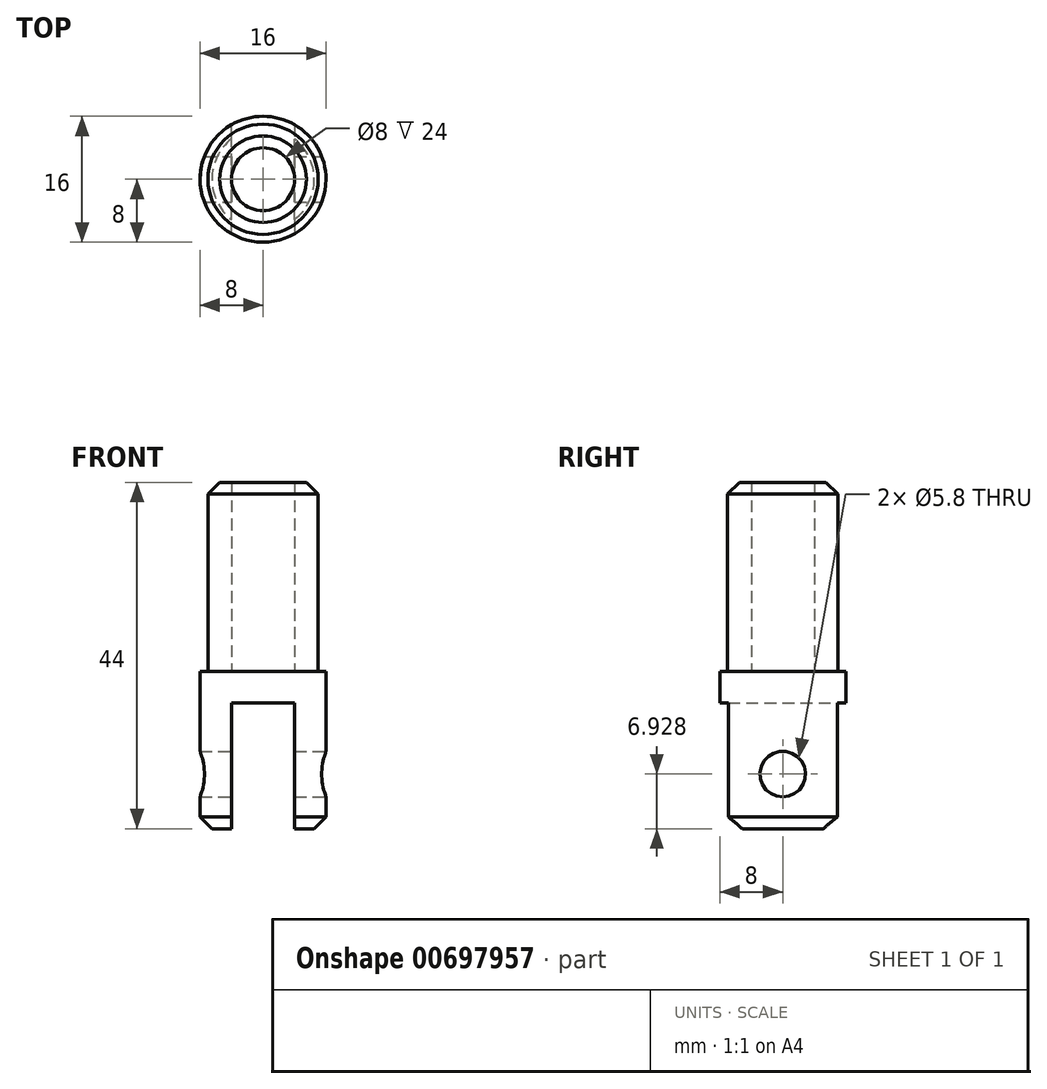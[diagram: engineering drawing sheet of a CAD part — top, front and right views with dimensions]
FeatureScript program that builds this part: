
annotation { "Feature Type Name" : "Feature", "Feature Type Description" : "" }
export const myFeature = defineFeature(function(context is Context, id is Id, definition is map)
    precondition{}
    {
        {
            assignVariable(context, id + "F0", {"name" : "d_r1", "anyValue" : 8});
        }
        {
            assignVariable(context, id + "F1", {"name" : "d_r2", "anyValue" : 14});
        }
        {
            assignVariable(context, id + "F2", {"name" : "d_r3", "anyValue" : 16});
        }
        {
            assignVariable(context, id + "F3", {"name" : "z_r1", "anyValue" : 1});
        }
        {
            assignVariable(context, id + "F4", {"name" : "z_r2", "anyValue" : 25});
        }
        {
            assignVariable(context, id + "F5", {"name" : "z_r3", "anyValue" : 1});
        }
        {
            assignVariable(context, id + "F6", {"name" : "z_baseplate", "anyValue" : 3});
        }
        {
            var Q0;
            Q0=qCreatedBy(makeId("Top.planeOp"),FACE);
            var sketch = newSketch(context, id + "F7", { "sketchPlane" : qUnion([Q0])});
            skCircle(sketch, "E0", {"center": v(0, 0) * mm, "radius": 4 * mm});
            skCircle(sketch, "E1", {"center": v(0, 0) * mm, "radius": 7 * mm});
            skCircle(sketch, "E2", {"center": v(0, 0) * mm, "radius": 8 * mm});
            skSolve(sketch);
        }
        {
            var Q0;
            Q0=makeQuery(id+"F7.imprint","IMPRINT",FACE,{"disambiguationData":[TD([[makeQuery(id+"F7.imprint","IMPRINT",EDGE,{"derivedFrom":sQuery(id+"F7.wireOp",EDGE,"E0")}),-1.0]])]});
            extrude(context, id + "F8", {"entities" : qUnion([Q0]), "depth" : (getVariable(context, 'z_r2')) * mm, "offsetDistance" : 25 * mm});
        }
        {
            var Q0;
            Q0=makeQuery(id+"F7.imprint","IMPRINT",FACE,{"disambiguationData":[TD([[makeQuery(id+"F7.imprint","IMPRINT",EDGE,{"derivedFrom":sQuery(id+"F7.wireOp",EDGE,"E0")}),1.0]])]});
            extrude(context, id + "F9", {"entities" : qUnion([Q0]), "operationType" : NewBodyOperationType.ADD, "depth" : (getVariable(context, 'z_r1')) * mm, "offsetDistance" : 25 * mm});
        }
        {
            var Q0;
            Q0=makeQuery(id+"F7.imprint","IMPRINT",FACE,{"disambiguationData":[TD([[makeQuery(id+"F7.imprint","IMPRINT",EDGE,{"derivedFrom":sQuery(id+"F7.wireOp",EDGE,"E1")}),-1.0]])]});
            extrude(context, id + "F10", {"entities" : qUnion([Q0]), "operationType" : NewBodyOperationType.ADD, "depth" : (getVariable(context, 'z_r3')) * mm, "offsetDistance" : 25 * mm});
        }
        {
            var Q0;
            Q0=makeQuery(id+"F7.imprint","IMPRINT",FACE,{"disambiguationData":[TD([[makeQuery(id+"F7.imprint","IMPRINT",EDGE,{"derivedFrom":sQuery(id+"F7.wireOp",EDGE,"E1")}),-1.0]])]});
            var Q1;
            Q1=makeQuery(id+"F7.imprint","IMPRINT",FACE,{"disambiguationData":[TD([[makeQuery(id+"F7.imprint","IMPRINT",EDGE,{"derivedFrom":sQuery(id+"F7.wireOp",EDGE,"E0")}),-1.0]])]});
            var Q2;
            Q2=makeQuery(id+"F7.imprint","IMPRINT",FACE,{"disambiguationData":[TD([[makeQuery(id+"F7.imprint","IMPRINT",EDGE,{"derivedFrom":sQuery(id+"F7.wireOp",EDGE,"E0")}),1.0]])]});
            extrude(context, id + "F11", {"entities" : qUnion([Q0, Q1, Q2]), "operationType" : NewBodyOperationType.ADD, "oppositeDirection" : true, "depth" : (getVariable(context, 'z_baseplate')) * mm, "offsetDistance" : 25 * mm});
        }
        {
            var Q0;
            Q0=makeQuery(id+"F11.opExtrude","CAP_FACE",FACE,{"disambiguationData":[OSD([sQuery(id+"F7.wireOp",EDGE,"E2")])],"isStart":false});
            var sketch = newSketch(context, id + "F12", { "sketchPlane" : qUnion([Q0])});
            skLineSegment(sketch, "E3", {"start": v(-4, 6.93) * mm, "end": v(-4, -6.93) * mm});
            skLineSegment(sketch, "E4", {"start": v(4, 6.93) * mm, "end": v(4, -6.93) * mm});
            skLineSegment(sketch, "E5", {"start": v(0, 0) * mm, "end": v(-4, 0) * mm, "construction": true});
            skLineSegment(sketch, "E6", {"start": v(0, 0) * mm, "end": v(4, 0) * mm, "construction": true});
            skSolve(sketch);
        }
        {
            var Q0;
            {var subQ0=sQuery(id+"F12.wireOp",EDGE,"E3");Q0=makeQuery(id+"F12.imprint","IMPRINT",FACE,{"disambiguationData":[TD([[makeQuery(id+"F12.imprint","IMPRINT",EDGE,{"derivedFrom":subQ0}),-1.0]])]});}
            var Q1;
            {var subQ0=sQuery(id+"F12.wireOp",EDGE,"E4");Q1=makeQuery(id+"F12.imprint","IMPRINT",FACE,{"disambiguationData":[TD([[makeQuery(id+"F12.imprint","IMPRINT",EDGE,{"derivedFrom":subQ0}),1.0]])]});}
            extrude(context, id + "F13", {"entities" : qUnion([Q0, Q1]), "operationType" : NewBodyOperationType.ADD, "depth" : (getVariable(context, 'd_r3')) * mm, "offsetDistance" : 25 * mm});
        }
        {
            var Q0;
            Q0=qCreatedBy(makeId("Right.planeOp"),FACE);
            var sketch = newSketch(context, id + "F14", { "sketchPlane" : qUnion([Q0])});
            skLineSegment(sketch, "E7.0", {"start": v(-6.93, -19) * mm, "end": v(6.93, -19) * mm});
            skCircle(sketch, "E8", {"center": v(0, -12.07) * mm, "radius": 6.93 * mm});
            skPoint(sketch, "E8.centerSnap0", {"position": v(0, -19) * mm});
            skLineSegment(sketch, "E9.0", {"start": v(-6.93, -19) * mm, "end": v(-6.93, -3) * mm});
            skLineSegment(sketch, "E9.1", {"start": v(6.93, -19) * mm, "end": v(6.93, -3) * mm});
            skLineSegment(sketch, "E10", {"start": v(-6.93, -3) * mm, "end": v(6.93, -3) * mm});
            skCircle(sketch, "E11", {"center": v(0, -12.07) * mm, "radius": 2.9 * mm});
            skSolve(sketch);
        }
        {
            var Q0;
            Q0=makeQuery(id+"F14.imprint","IMPRINT",FACE,{"disambiguationData":[TD([[makeQuery(id+"F14.imprint","IMPRINT",EDGE,{"derivedFrom":sQuery(id+"F14.wireOp",EDGE,"E11")}),1.0]])]});
            extrude(context, id + "F15", {"entities" : qUnion([Q0]), "operationType" : NewBodyOperationType.REMOVE, "endBound" : BoundingType.SYMMETRIC, "oppositeDirection" : true, "depth" : 25 * mm, "offsetDistance" : 25 * mm});
        }
        {
            var Q0;
            Q0=makeQuery(id+"F8.opExtrude","CAP_EDGE",EDGE,{"disambiguationData":[OSD([sQuery(id+"F7.wireOp",EDGE,"E1")])],"isStart":false});
            var Q1;
            Q1=makeQuery(id+"F13.opExtrude","CAP_EDGE",EDGE,{"disambiguationData":[OSD([sQuery(id+"F12.wireOp",EDGE,"E4")])],"isStart":true});
            var Q2;
            Q2=makeQuery(id+"F13.opExtrude","CAP_EDGE",EDGE,{"disambiguationData":[OSD([sQuery(id+"F12.wireOp",EDGE,"E3")])],"isStart":true});
            var Q3;
            {var subQ0=sQuery(id+"F12.wireOp",EDGE,"E4");var subQ1=sQuery(id+"F7.wireOp",EDGE,"E2");var subQ2=makeQuery(id+"F11.opExtrude","CAP_EDGE",EDGE,{"disambiguationData":[OSD([subQ1])],"isStart":false});Q3=makeQuery(id+"F13.opExtrude","CAP_EDGE",EDGE,{"disambiguationData":[OSD([subQ1]),TDD([makeQuery(id+"F12.imprint","IMPRINT",EDGE,{"disambiguationData":[TD([[makeQuery(id+"F12.imprint","INTERSECT",VERTEX,{"disambiguationData":[OD(0.0)],"derivedFrom":[subQ2,subQ0]}),-1.0]])],"derivedFrom":subQ2})])],"isStart":false});}
            var Q4;
            {var subQ0=sQuery(id+"F12.wireOp",EDGE,"E3");var subQ1=sQuery(id+"F7.wireOp",EDGE,"E2");var subQ2=makeQuery(id+"F11.opExtrude","CAP_EDGE",EDGE,{"disambiguationData":[OSD([subQ1])],"isStart":false});Q4=makeQuery(id+"F13.opExtrude","CAP_EDGE",EDGE,{"disambiguationData":[OSD([subQ1]),TDD([makeQuery(id+"F12.imprint","IMPRINT",EDGE,{"disambiguationData":[TD([[makeQuery(id+"F12.imprint","INTERSECT",VERTEX,{"disambiguationData":[OD(0.0)],"derivedFrom":[subQ2,subQ0]}),1.0]])],"derivedFrom":subQ2})])],"isStart":false});}
            chamfer(context, id + "F16", {"entities" : qUnion([Q0, Q1, Q2, Q3, Q4]), "width" : ((getVariable(context, 'd_r2') - getVariable(context, 'd_r1')) / 4) * mm, "tangentPropagation" : true});
        }
    });
